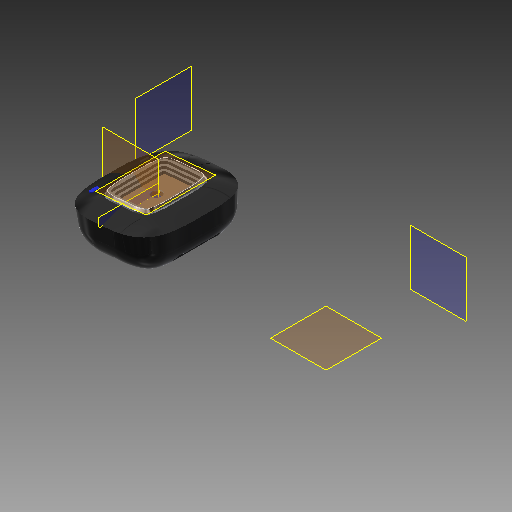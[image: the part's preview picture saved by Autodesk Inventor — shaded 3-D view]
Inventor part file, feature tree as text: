
AUTODESK INVENTOR PART (.ipt)
format: ipt  version: 2017 (Build 210142000, 142)  size: 1,796,096 bytes
history: native  units: mm
features: sketch x18, extrude x13, plane x12, fillet x6, sweep x5, other x5, thicken_offset x4, mirror x3, projected_geometry x3
ambient origin geometry x8: Origin, YZ Plane, XZ Plane, XY Plane, X Axis, Y Axis, Z Axis, Center Point
bodies: Body1 (feature_tree), Body2 (feature_tree), Body3 (feature_tree), Body4 (feature_tree), Body5 (feature_tree)
feature tree (69):
  sketch  "Sketch1"  dims[d0=109.0mm d1=44.5mm d189=90.0deg]
  plane  "Work Plane8"
  plane  "Work Plane7"
  sketch  "Sketch3"  dims[d190=3.0mm d193=0.0mm d194=0.0mm]
  plane  "Work Plane6"
  plane  "Work Plane1"
  sketch  "Sketch5"  dims[d201=0.5mm d202=0.5mm]
  plane  "Work Plane2"
  sketch  "Sketch6"  dims[d204=0.5mm d205=0.2mm]
  plane  "Work Plane5"
  sketch  "Sketch8"  dims[d210=15.0mm d211=-0.872665mm d212=10.0mm]
  mirror  "Mirror1"
  thicken_offset  "Thicken1"
  thicken_offset  "Thicken2"
  mirror  "Mirror3"
  thicken_offset  "Thicken4"
  thicken_offset  "Thicken5"
  extrude  "Extrusion6"  Depth=44.5mm
  fillet  "Fillet1"  [1 undecoded]
  sketch  "Sketch12"  dims[d220=5.0mm d221=0.0mm d224=-1.0mm]
  plane  "Work Plane9"
  sweep  "Sweep1"
  mirror  "Mirror4"
  plane  "Work Plane11"
  extrude  "Extrusion9"  Depth=0.5mm
  plane  "Work Plane13"
  extrude  "Extrusion10"  Depth=0.2mm
  plane  "Work Plane14"
  extrude  "Extrusion11"  Depth=10.0mm
  plane  "Work Plane15"
  extrude  "Extrusion12"  [1 undecoded]
  plane  "Work Plane16"
  sketch  "Sketch20"  dims[d242=1.0mm d243=1.0mm]
  extrude  "Extrusion13"  [1 undecoded]
  extrude  "Extrusion15"  Depth=11.0mm
  sketch  "Sketch21"  dims[d245=1.0mm d246=1.0mm d247=1.0mm d248=0.0mm d249=0.0mm]
  extrude  "Extrusion16"  Depth=8.0mm
  fillet  "Fillet2"  Radius=2.0mm
  sketch  "Sketch22"  dims[d250=3.0mm d251=0.0mm d255=2.75mm d256=0.0mm]
  extrude  "Extrusion17"  [1 undecoded]
  extrude  "Extrusion18"  Depth=6.0mm TaperAngle=0.0deg
  fillet  "Fillet3"  [1 undecoded]
  extrude  "Extrusion19"  Depth=1.0mm
  fillet  "Fillet4"  Radius=1.0mm
  extrude  "Extrusion20"  Depth=1.0mm
  extrude  "Extrusion21"  Depth=1.0mm
  fillet  "Fillet5"  Radius=1.0mm
  fillet  "Fillet6"  [1 undecoded]
  other  "Image4"
  other  "Srf3"
  other  "Srf4"
  other  "Srf7"
  other  "Srf8"
  sketch  "Sketch11"  dims[d213=0.0mm d214=0.0mm d219=-0.5mm]
  sketch  "Sketch13"  dims[d225=22.0mm d226=11.0mm]
  sketch  "Sketch15"  dims[d227=16.0mm d228=8.0mm d229=2.0mm]
  projected_geometry  "Projected Loop7"
  sketch  "Sketch17"  dims[d230=1.0mm d231=0.0mm d232=-1.0mm]
  sketch  "Sketch18"  dims[d233=1.0mm d234=6.0mm d235=0.0mm d236=-1.0mm]
  sketch  "Sketch19"  dims[d237=1.0mm d240=1.0mm d241=1.0mm]
  sketch  "Sketch23"  dims[d257=2.0mm d258=0.0mm d259=0.1mm]
  sketch  "Sketch24"  dims[d260=2.1mm d261=0.0mm d262=2.75mm d263=0.0mm]
  sketch  "Sketch25"  dims[d264=0.1mm d265=1.5mm d266=0.0mm d267=0.5mm d268=10.0mm d269=0.0mm d270=5.0mm d271=5.0mm d272=0.0mm d273=3.0mm d274=0.5mm d275=15.0mm d276=14.0mm]
  projected_geometry  "Projected Loop10"
  sweep  "SweepSrf1"
  sweep  "SweepSrf2"
  sweep  "SweepSrf5"
  sweep  "SweepSrf6"
  projected_geometry  "Project Cut Edges1"
note: 6 required parameter values undecoded (feature->parameter linkage not recoverable at this tier; creation-order binding heuristic only, values carry confidence <= 0.55)
